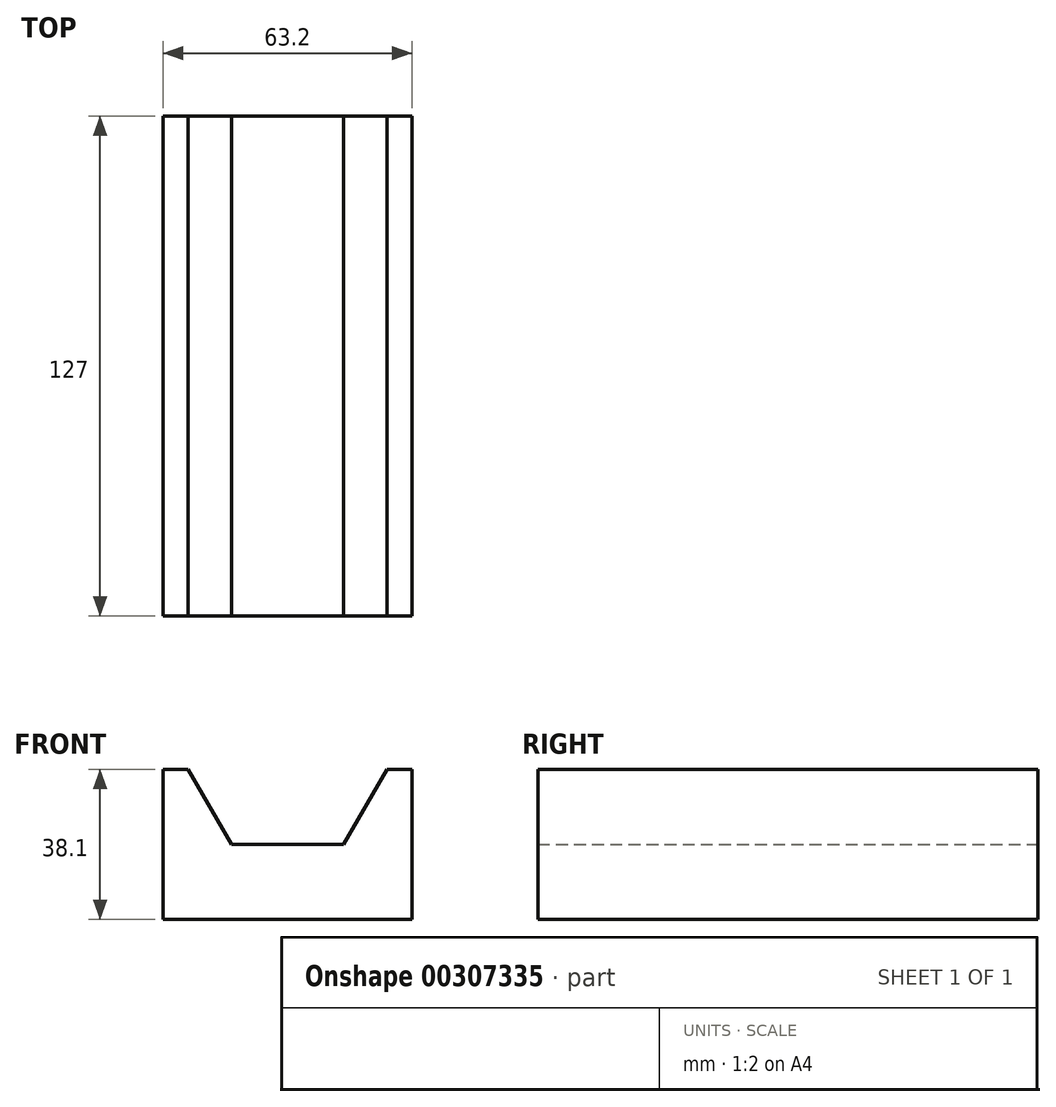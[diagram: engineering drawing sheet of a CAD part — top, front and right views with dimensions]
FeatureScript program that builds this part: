
annotation { "Feature Type Name" : "Feature", "Feature Type Description" : "" }
export const myFeature = defineFeature(function(context is Context, id is Id, definition is map)
    precondition{}
    {
        {
            var Q0;
            Q0=qCreatedBy(makeId("Front.planeOp"),FACE);
            var sketch = newSketch(context, id + "F0", { "sketchPlane" : qUnion([Q0])});
            skLineSegment(sketch, "E0", {"start": v(-54.56, 23.2) * mm, "end": v(-54.56, 4.15) * mm});
            skLineSegment(sketch, "E1", {"start": v(-37.21, 4.15) * mm, "end": v(-8.71, 4.15) * mm});
            skLineSegment(sketch, "E2", {"start": v(8.64, 4.15) * mm, "end": v(8.64, 23.2) * mm});
            skLineSegment(sketch, "E3", {"start": v(-54.56, 4.15) * mm, "end": v(-54.56, -14.9) * mm});
            skLineSegment(sketch, "E4", {"start": v(-54.56, -14.9) * mm, "end": v(8.64, -14.9) * mm});
            skLineSegment(sketch, "E5", {"start": v(8.64, -14.9) * mm, "end": v(8.64, 4.15) * mm});
            skLineSegment(sketch, "E6", {"start": v(-54.56, 23.2) * mm, "end": v(-48.2, 23.2) * mm});
            skLineSegment(sketch, "E7", {"start": v(-48.2, 23.2) * mm, "end": v(-37.21, 4.15) * mm});
            skLineSegment(sketch, "E8", {"start": v(8.64, 23.2) * mm, "end": v(2.29, 23.2) * mm});
            skLineSegment(sketch, "E9", {"start": v(2.29, 23.2) * mm, "end": v(-8.71, 4.15) * mm});
            skSolve(sketch);
        }
        {
            var Q0;
            Q0 = qSketchRegion(id + "F0", true);
            extrude(context, id + "F1", {"entities" : qUnion([Q0]), "depth" : 127 * mm});
        }
    });
